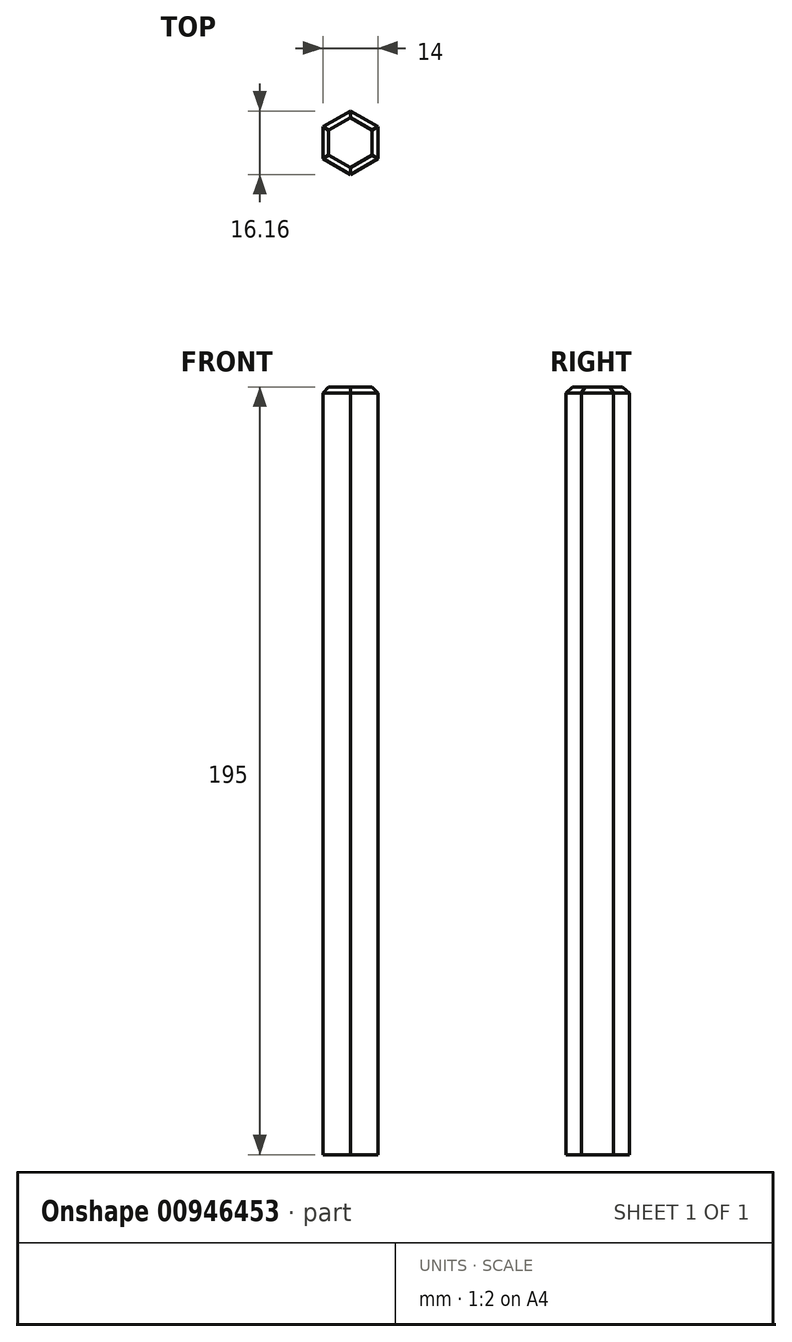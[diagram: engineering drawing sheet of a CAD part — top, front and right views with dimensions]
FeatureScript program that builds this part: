
annotation { "Feature Type Name" : "Feature", "Feature Type Description" : "" }
export const myFeature = defineFeature(function(context is Context, id is Id, definition is map)
    precondition{}
    {
        {
            var Q0;
            Q0=qCreatedBy(makeId("Top.planeOp"),FACE);
            var sketch = newSketch(context, id + "F0", { "sketchPlane" : qUnion([Q0])});
            skCircle(sketch, "E0.cCircle", {"center": v(0, 0) * mm, "radius": 7 * mm, "construction": true});
            skLineSegment(sketch, "E0.0", {"start": v(7, 4.04) * mm, "end": v(7, -4.04) * mm});
            skLineSegment(sketch, "E0.1", {"start": v(7, -4.04) * mm, "end": v(0, -8.08) * mm});
            skLineSegment(sketch, "E0.2", {"start": v(0, -8.08) * mm, "end": v(-7, -4.04) * mm});
            skLineSegment(sketch, "E0.3", {"start": v(-7, -4.04) * mm, "end": v(-7, 4.04) * mm});
            skLineSegment(sketch, "E0.4", {"start": v(-7, 4.04) * mm, "end": v(0, 8.08) * mm});
            skLineSegment(sketch, "E0.5", {"start": v(0, 8.08) * mm, "end": v(7, 4.04) * mm});
            skPoint(sketch, "E0.0.midPoint", {"position": v(7, 0) * mm});
            skSolve(sketch);
        }
        {
            var Q0;
            Q0 = qSketchRegion(id + "F0", true);
            extrude(context, id + "F1", {"entities" : qUnion([Q0]), "depth" : 195 * mm, "offsetDistance" : 25 * mm});
        }
        {
            var Q0;
            Q0=makeQuery(id+"F1.opExtrude","CAP_EDGE",EDGE,{"disambiguationData":[OSD([sQuery(id+"F0.wireOp",EDGE,"E0.2")])],"isStart":false});
            var Q1;
            Q1=makeQuery(id+"F1.opExtrude","CAP_EDGE",EDGE,{"disambiguationData":[OSD([sQuery(id+"F0.wireOp",EDGE,"E0.1")])],"isStart":false});
            var Q2;
            Q2=makeQuery(id+"F1.opExtrude","CAP_EDGE",EDGE,{"disambiguationData":[OSD([sQuery(id+"F0.wireOp",EDGE,"E0.0")])],"isStart":false});
            var Q3;
            Q3=makeQuery(id+"F1.opExtrude","CAP_EDGE",EDGE,{"disambiguationData":[OSD([sQuery(id+"F0.wireOp",EDGE,"E0.5")])],"isStart":false});
            var Q4;
            Q4=makeQuery(id+"F1.opExtrude","CAP_EDGE",EDGE,{"disambiguationData":[OSD([sQuery(id+"F0.wireOp",EDGE,"E0.4")])],"isStart":false});
            var Q5;
            Q5=makeQuery(id+"F1.opExtrude","CAP_EDGE",EDGE,{"disambiguationData":[OSD([sQuery(id+"F0.wireOp",EDGE,"E0.3")])],"isStart":false});
            chamfer(context, id + "F2", {"entities" : qUnion([Q0, Q1, Q2, Q3, Q4, Q5]), "width" : 1.5 * mm, "tangentPropagation" : true});
        }
    });
